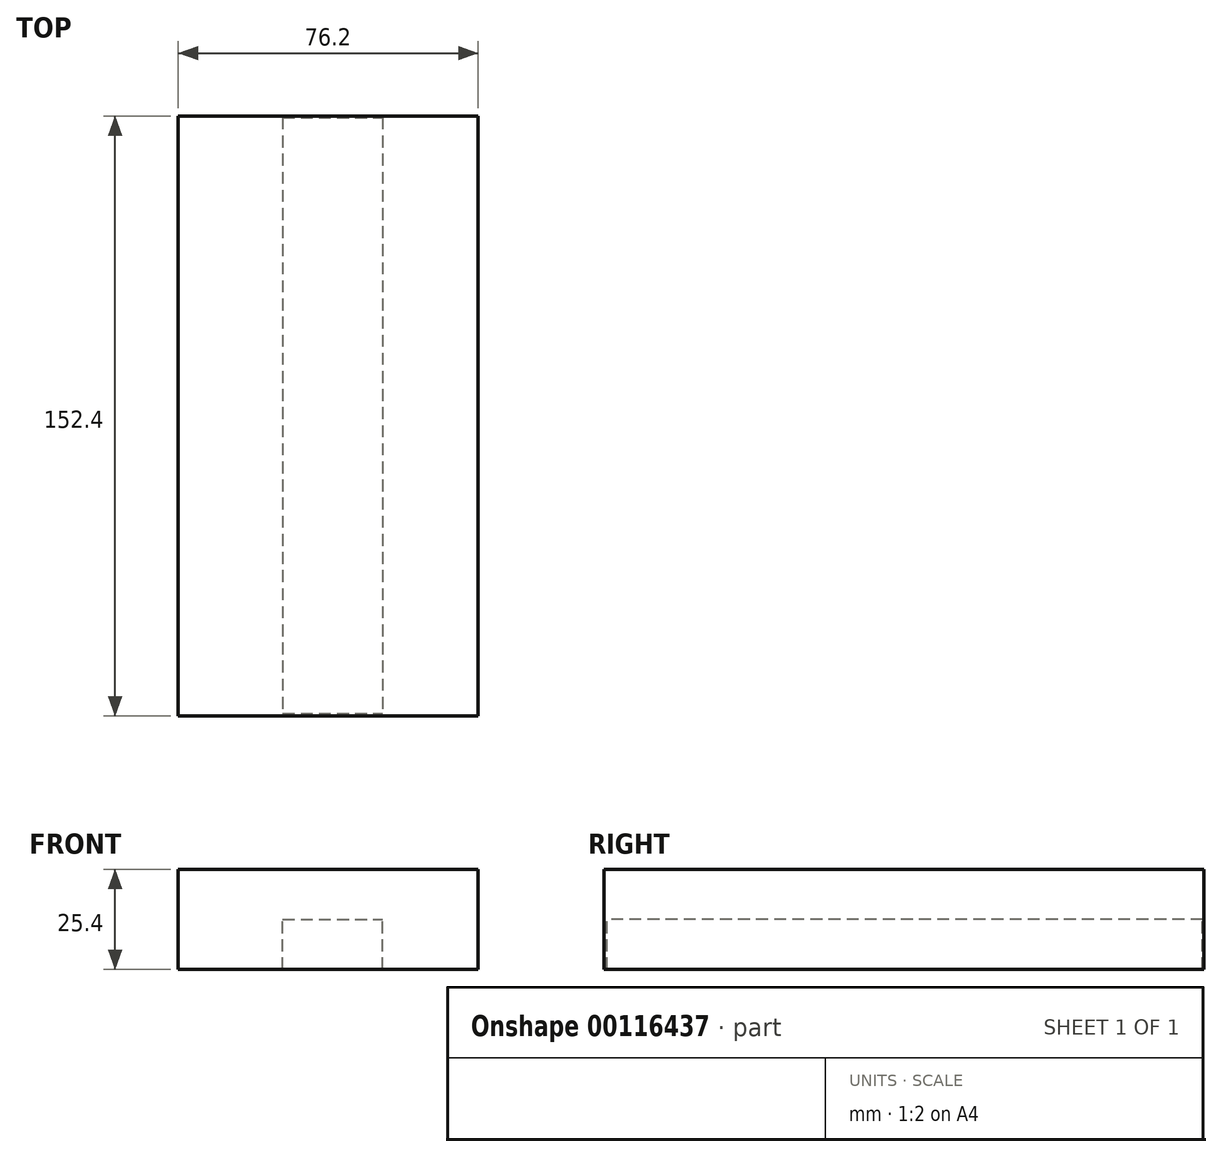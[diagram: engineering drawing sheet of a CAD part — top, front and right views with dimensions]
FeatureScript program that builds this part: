
annotation { "Feature Type Name" : "Feature", "Feature Type Description" : "" }
export const myFeature = defineFeature(function(context is Context, id is Id, definition is map)
    precondition{}
    {
        {
            var Q0;
            Q0=qCreatedBy(makeId("Top.planeOp"),FACE);
            var sketch = newSketch(context, id + "F0", { "sketchPlane" : qUnion([Q0])});
            skLineSegment(sketch, "E0.bottom", {"start": v(-102.94, 128.13) * mm, "end": v(-26.74, 128.13) * mm});
            skLineSegment(sketch, "E0.top", {"start": v(-102.94, -24.27) * mm, "end": v(-26.74, -24.27) * mm});
            skLineSegment(sketch, "E0.left", {"start": v(-102.94, 128.13) * mm, "end": v(-102.94, -24.27) * mm});
            skLineSegment(sketch, "E0.right", {"start": v(-26.74, 128.13) * mm, "end": v(-26.74, -24.27) * mm});
            skLineSegment(sketch, "E1.bottom", {"start": v(-78.57, 128.13) * mm, "end": v(-53.17, 128.13) * mm});
            skLineSegment(sketch, "E1.top", {"start": v(-78.57, -24.27) * mm, "end": v(-53.17, -24.27) * mm});
            skSolve(sketch);
        }
        {
            var Q0;
            Q0 = qSketchRegion(id + "F0", true);
            extrude(context, id + "F1", {"entities" : qUnion([Q0]), "depth" : 25.4 * mm});
        }
        {
            var Q0;
            Q0=qCreatedBy(makeId("Top.planeOp"),FACE);
            var sketch = newSketch(context, id + "F2", { "sketchPlane" : qUnion([Q0])});
            skLineSegment(sketch, "E2.bottom", {"start": v(-76.39, 127.77) * mm, "end": v(-50.99, 127.77) * mm});
            skLineSegment(sketch, "E2.top", {"start": v(-76.39, -23.6) * mm, "end": v(-50.99, -23.6) * mm});
            skLineSegment(sketch, "E2.left", {"start": v(-76.39, 127.77) * mm, "end": v(-76.39, -23.6) * mm});
            skLineSegment(sketch, "E2.right", {"start": v(-50.99, 127.77) * mm, "end": v(-50.99, -23.6) * mm});
            skSolve(sketch);
        }
        {
            var Q0;
            Q0 = qSketchRegion(id + "F2", true);
            extrude(context, id + "F3", {"entities" : qUnion([Q0]), "operationType" : NewBodyOperationType.REMOVE, "oppositeDirection" : true, "depth" : 25.4 * mm, "hasSecondDirection" : true, "secondDirectionOppositeDirection" : false, "secondDirectionDepth" : 12.7 * mm});
        }
    });
